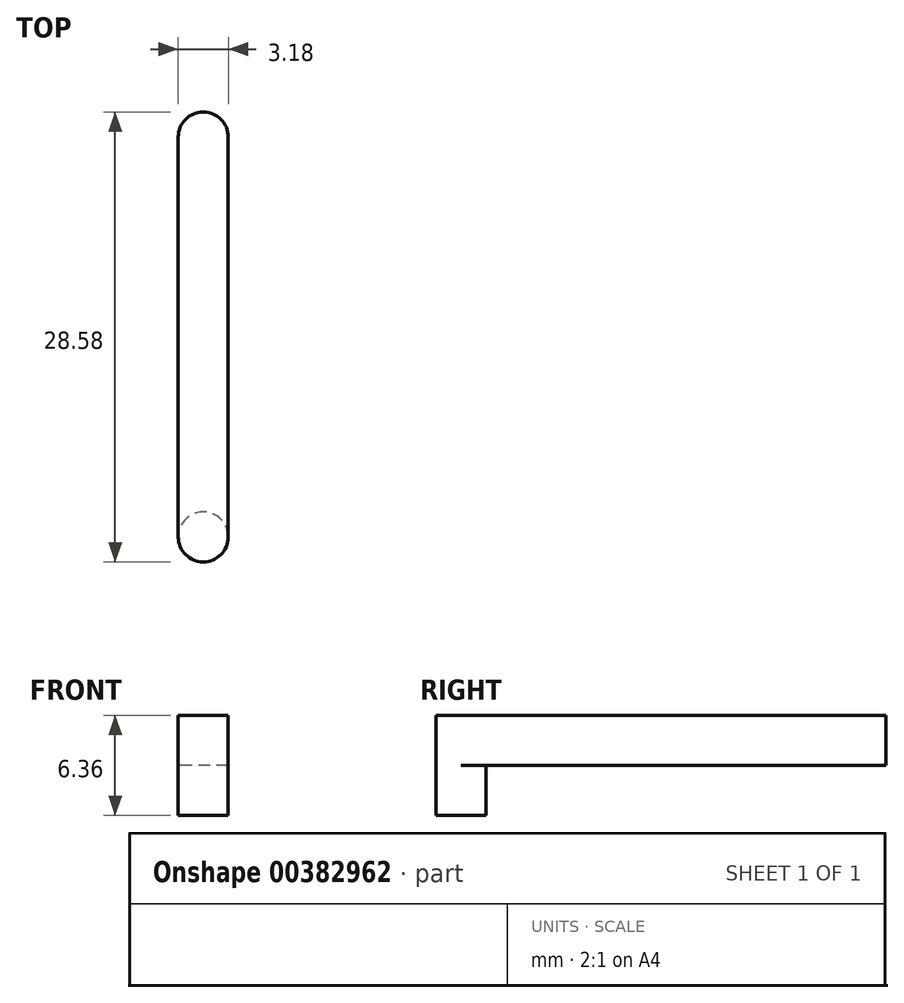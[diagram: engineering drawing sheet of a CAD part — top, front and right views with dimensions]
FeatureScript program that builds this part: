
annotation { "Feature Type Name" : "Feature", "Feature Type Description" : "" }
export const myFeature = defineFeature(function(context is Context, id is Id, definition is map)
    precondition{}
    {
        {
            var Q0;
            Q0=qCreatedBy(makeId("Top.planeOp"),FACE);
            var sketch = newSketch(context, id + "F0", { "sketchPlane" : qUnion([Q0])});
            skLineSegment(sketch, "E0.bottom", {"start": v(-1.59, 12.7) * mm, "end": v(1.59, 12.7) * mm});
            skLineSegment(sketch, "E0.top", {"start": v(-1.59, -12.7) * mm, "end": v(1.59, -12.7) * mm});
            skLineSegment(sketch, "E0.left", {"start": v(-1.59, 12.7) * mm, "end": v(-1.59, -12.7) * mm});
            skLineSegment(sketch, "E0.right", {"start": v(1.59, 12.7) * mm, "end": v(1.59, -12.7) * mm});
            skPoint(sketch, "E0.middle", {"position": v(0, 0) * mm});
            skArc(sketch, "E1", {"start": v(-1.59, -12.7) * mm, "mid": v(0, -14.29) * mm, "end": v(1.59, -12.7) * mm});
            skArc(sketch, "E2", {"start": v(1.59, 12.7) * mm, "mid": v(0, 14.29) * mm, "end": v(-1.59, 12.7) * mm});
            skCircle(sketch, "E3", {"center": v(0, 12.7) * mm, "radius": 1.59 * mm});
            skCircle(sketch, "E4", {"center": v(0, -12.7) * mm, "radius": 1.59 * mm});
            skSolve(sketch);
        }
        {
            var Q0;
            {var subQ1=sQuery(id+"F0.wireOp",EDGE,"E0.left");Q0=makeQuery(id+"F0.imprint","IMPRINT",FACE,{"disambiguationData":[TD([[makeQuery(id+"F0.imprint","IMPRINT",EDGE,{"derivedFrom":subQ1}),1.0]])]});}
            var Q1;
            {var subQ0=sQuery(id+"F0.wireOp",EDGE,"E4");var subQ1=sQuery(id+"F0.wireOp",EDGE,"E0.top");var subQ2=makeQuery(id+"F0.imprint","INTERSECT",VERTEX,{"disambiguationData":[OD(0.0)],"derivedFrom":[subQ1,subQ0]});Q1=makeQuery(id+"F0.imprint","IMPRINT",FACE,{"disambiguationData":[TD([[makeQuery(id+"F0.imprint","IMPRINT",EDGE,{"disambiguationData":[TD([[subQ2,-1.0]])],"derivedFrom":subQ1}),1.0]])]});}
            var Q2;
            {var subQ0=sQuery(id+"F0.wireOp",EDGE,"E4");var subQ1=sQuery(id+"F0.wireOp",EDGE,"E0.top");var subQ2=makeQuery(id+"F0.imprint","INTERSECT",VERTEX,{"disambiguationData":[OD(0.0)],"derivedFrom":[subQ1,subQ0]});Q2=makeQuery(id+"F0.imprint","IMPRINT",FACE,{"disambiguationData":[TD([[makeQuery(id+"F0.imprint","IMPRINT",EDGE,{"disambiguationData":[TD([[subQ2,-1.0]])],"derivedFrom":subQ1}),-1.0]])]});}
            var Q3;
            {var subQ0=sQuery(id+"F0.wireOp",EDGE,"E1");Q3=makeQuery(id+"F0.imprint","IMPRINT",FACE,{"disambiguationData":[TD([[makeQuery(id+"F0.imprint","IMPRINT",EDGE,{"derivedFrom":subQ0}),1.0]])]});}
            var Q4;
            {var subQ0=sQuery(id+"F0.wireOp",EDGE,"E2");Q4=makeQuery(id+"F0.imprint","IMPRINT",FACE,{"disambiguationData":[TD([[makeQuery(id+"F0.imprint","IMPRINT",EDGE,{"derivedFrom":subQ0}),1.0]])]});}
            var Q5;
            {var subQ0=sQuery(id+"F0.wireOp",EDGE,"E3");var subQ1=sQuery(id+"F0.wireOp",EDGE,"E0.bottom");var subQ2=makeQuery(id+"F0.imprint","INTERSECT",VERTEX,{"disambiguationData":[OD(0.0)],"derivedFrom":[subQ1,subQ0]});Q5=makeQuery(id+"F0.imprint","IMPRINT",FACE,{"disambiguationData":[TD([[makeQuery(id+"F0.imprint","IMPRINT",EDGE,{"disambiguationData":[TD([[subQ2,-1.0]])],"derivedFrom":subQ1}),1.0]])]});}
            var Q6;
            {var subQ0=sQuery(id+"F0.wireOp",EDGE,"E3");var subQ1=sQuery(id+"F0.wireOp",EDGE,"E0.bottom");var subQ2=makeQuery(id+"F0.imprint","INTERSECT",VERTEX,{"disambiguationData":[OD(0.0)],"derivedFrom":[subQ1,subQ0]});Q6=makeQuery(id+"F0.imprint","IMPRINT",FACE,{"disambiguationData":[TD([[makeQuery(id+"F0.imprint","IMPRINT",EDGE,{"disambiguationData":[TD([[subQ2,-1.0]])],"derivedFrom":subQ1}),-1.0]])]});}
            extrude(context, id + "F1", {"entities" : qUnion([Q0, Q1, Q2, Q3, Q4, Q5, Q6]), "depth" : 3.17 * mm});
        }
        {
            var Q0;
            {var subQ0=sQuery(id+"F0.wireOp",EDGE,"E4");var subQ1=sQuery(id+"F0.wireOp",EDGE,"E0.top");var subQ2=makeQuery(id+"F0.imprint","INTERSECT",VERTEX,{"disambiguationData":[OD(0.0)],"derivedFrom":[subQ1,subQ0]});Q0=makeQuery(id+"F0.imprint","IMPRINT",FACE,{"disambiguationData":[TD([[makeQuery(id+"F0.imprint","IMPRINT",EDGE,{"disambiguationData":[TD([[subQ2,-1.0]])],"derivedFrom":subQ1}),-1.0]])]});}
            var Q1;
            {var subQ0=sQuery(id+"F0.wireOp",EDGE,"E4");var subQ1=sQuery(id+"F0.wireOp",EDGE,"E0.top");var subQ2=makeQuery(id+"F0.imprint","INTERSECT",VERTEX,{"disambiguationData":[OD(0.0)],"derivedFrom":[subQ1,subQ0]});Q1=makeQuery(id+"F0.imprint","IMPRINT",FACE,{"disambiguationData":[TD([[makeQuery(id+"F0.imprint","IMPRINT",EDGE,{"disambiguationData":[TD([[subQ2,-1.0]])],"derivedFrom":subQ1}),1.0]])]});}
            extrude(context, id + "F2", {"entities" : qUnion([Q0, Q1]), "operationType" : NewBodyOperationType.ADD, "oppositeDirection" : true, "depth" : 3.17 * mm});
        }
    });
